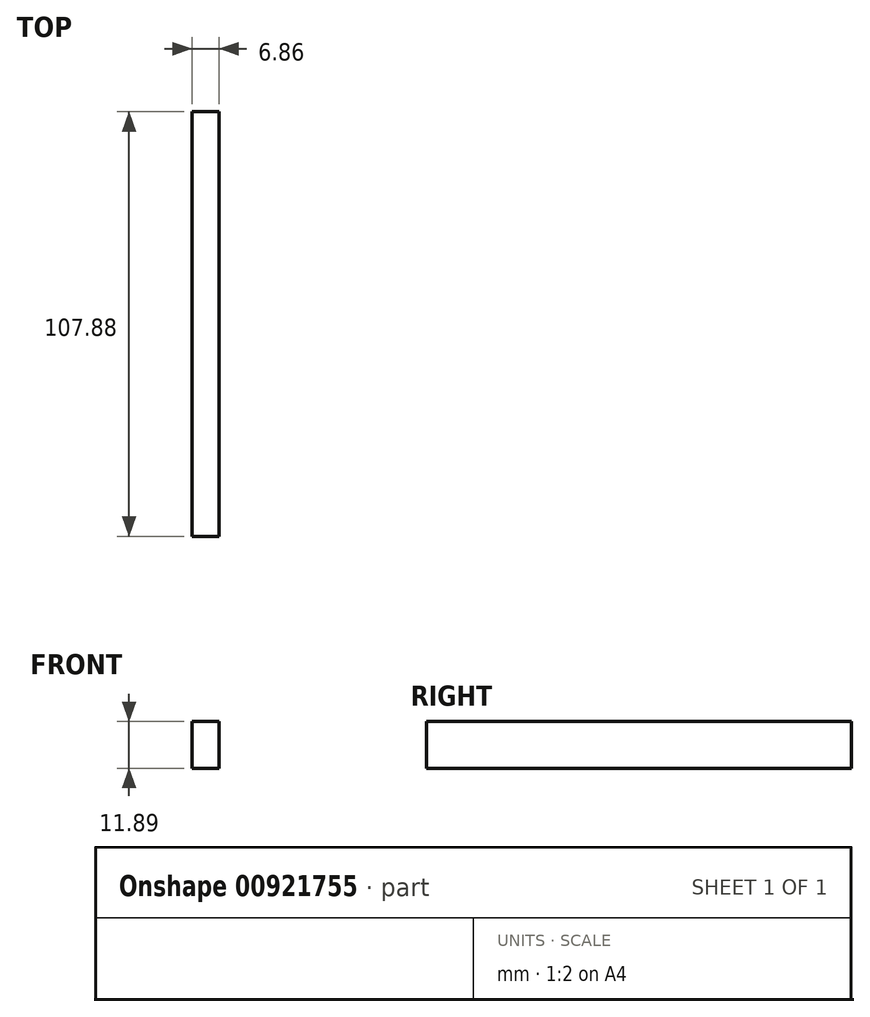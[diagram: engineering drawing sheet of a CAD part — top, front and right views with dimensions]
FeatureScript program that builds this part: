
annotation { "Feature Type Name" : "Feature", "Feature Type Description" : "" }
export const myFeature = defineFeature(function(context is Context, id is Id, definition is map)
    precondition{}
    {
        {
            var Q0;
            Q0=qCreatedBy(makeId("Front.planeOp"),FACE);
            var sketch = newSketch(context, id + "F0", { "sketchPlane" : qUnion([Q0])});
            skLineSegment(sketch, "E0.bottom", {"start": v(-45.98, 31.42) * mm, "end": v(-39.12, 31.42) * mm});
            skLineSegment(sketch, "E0.top", {"start": v(-45.98, 19.53) * mm, "end": v(-39.12, 19.53) * mm});
            skLineSegment(sketch, "E0.left", {"start": v(-45.98, 31.42) * mm, "end": v(-45.98, 19.53) * mm});
            skLineSegment(sketch, "E0.right", {"start": v(-39.12, 31.42) * mm, "end": v(-39.12, 19.53) * mm});
            skSolve(sketch);
        }
        {
            var Q0;
            Q0 = qSketchRegion(id + "F0", true);
            extrude(context, id + "F1", {"entities" : qUnion([Q0]), "depth" : 107.88 * mm, "offsetDistance" : 25.4 * mm});
        }
    });
